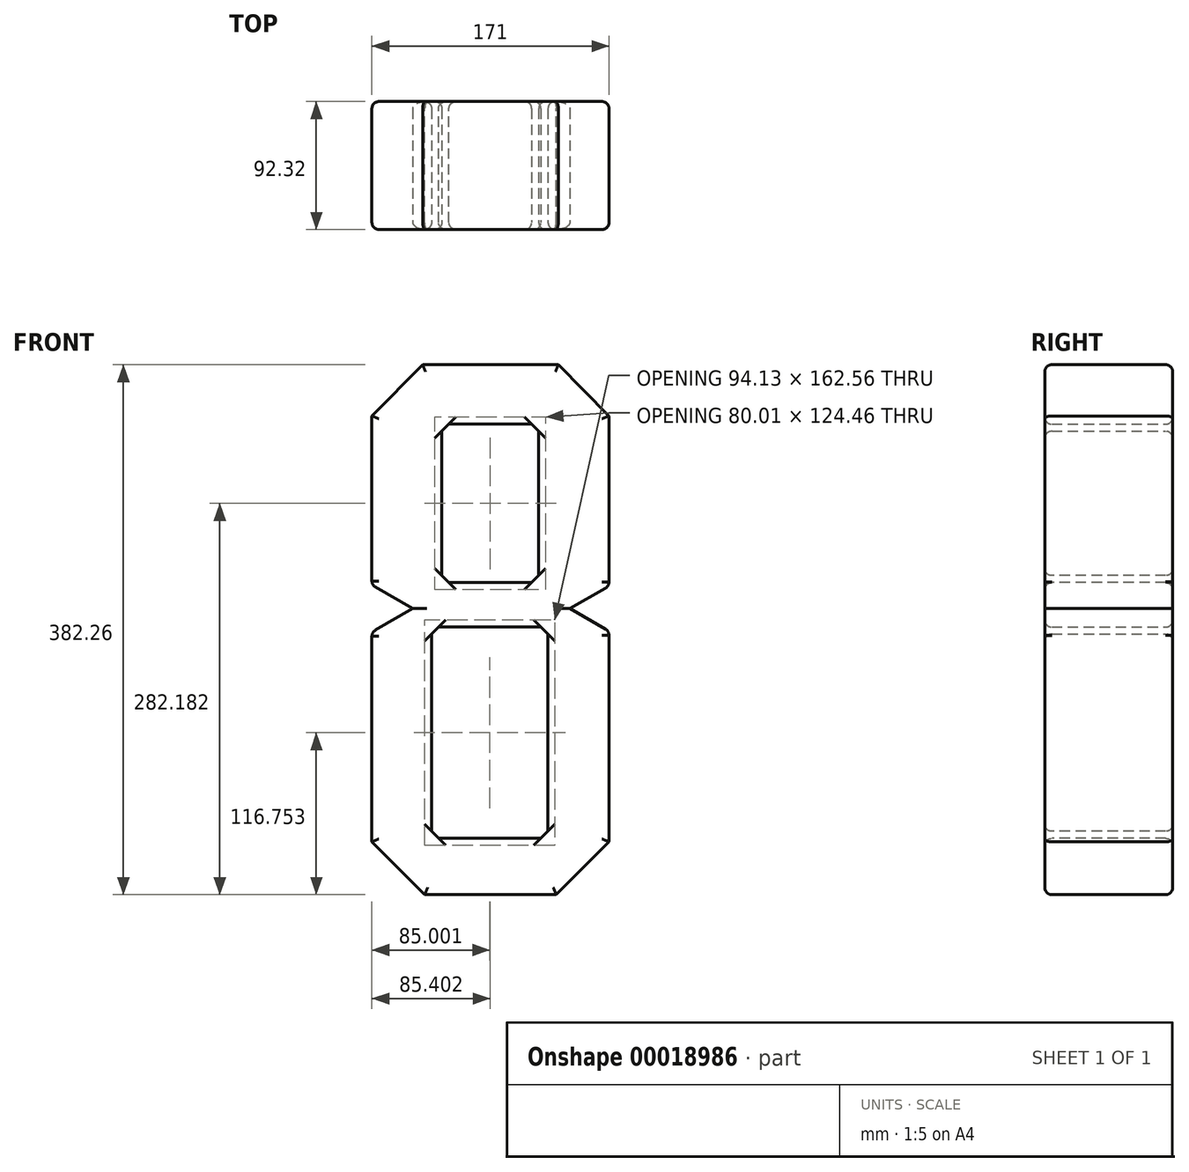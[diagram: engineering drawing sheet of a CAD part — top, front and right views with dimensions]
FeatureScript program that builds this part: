
annotation { "Feature Type Name" : "Feature", "Feature Type Description" : "" }
export const myFeature = defineFeature(function(context is Context, id is Id, definition is map)
    precondition{}
    {
        {
            var Q0;
            Q0=qCreatedBy(makeId("Top.planeOp"),FACE);
            var sketch = newSketch(context, id + "F0", { "sketchPlane" : qUnion([Q0])});
            skLineSegment(sketch, "E0.bottom", {"start": v(-73.79, 22.76) * mm, "end": v(97.2, 22.76) * mm});
            skLineSegment(sketch, "E0.top", {"start": v(-73.79, -22.31) * mm, "end": v(97.2, -22.31) * mm});
            skLineSegment(sketch, "E0.left", {"start": v(-73.79, 22.76) * mm, "end": v(-73.79, -22.31) * mm});
            skLineSegment(sketch, "E0.right", {"start": v(97.2, 22.76) * mm, "end": v(97.2, -22.31) * mm});
            skSolve(sketch);
        }
        {
            var Q0;
            Q0 = qSketchRegion(id + "F0", true);
            extrude(context, id + "F1", {"entities" : qUnion([Q0]), "depth" : 382.26 * mm});
        }
        {
            var Q0;
            Q0=makeQuery(id+"F1.opExtrude","SWEPT_FACE",FACE,{"disambiguationData":[OSD([sQuery(id+"F0.wireOp",EDGE,"E0.bottom")])]});
            var sketch = newSketch(context, id + "F2", { "sketchPlane" : qUnion([Q0])});
            skLineSegment(sketch, "E1.bottom", {"start": v(-46.54, 339.33) * mm, "end": v(23.31, 339.33) * mm});
            skLineSegment(sketch, "E1.top", {"start": v(-46.54, 225.03) * mm, "end": v(23.31, 225.03) * mm});
            skLineSegment(sketch, "E1.left", {"start": v(-46.54, 339.33) * mm, "end": v(-46.54, 225.03) * mm});
            skLineSegment(sketch, "E1.right", {"start": v(23.31, 339.33) * mm, "end": v(23.31, 225.03) * mm});
            skLineSegment(sketch, "E2.bottom", {"start": v(-53.2, 192.95) * mm, "end": v(30.77, 192.95) * mm});
            skLineSegment(sketch, "E2.top", {"start": v(-53.2, 40.55) * mm, "end": v(30.77, 40.55) * mm});
            skLineSegment(sketch, "E2.left", {"start": v(-53.2, 192.95) * mm, "end": v(-53.2, 40.55) * mm});
            skLineSegment(sketch, "E2.right", {"start": v(30.77, 192.95) * mm, "end": v(30.77, 40.55) * mm});
            skSolve(sketch);
        }
        {
            var Q0;
            Q0 = qSketchRegion(id + "F2", true);
            extrude(context, id + "F3", {"entities" : qUnion([Q0]), "operationType" : NewBodyOperationType.REMOVE, "endBound" : BoundingType.THROUGH_ALL, "oppositeDirection" : true, "depth" : 25.4 * mm});
        }
        {
            var Q0;
            Q0=makeQuery(id+"F1.opExtrude","SWEPT_FACE",FACE,{"disambiguationData":[OSD([sQuery(id+"F0.wireOp",EDGE,"E0.bottom")])]});
            var sketch = newSketch(context, id + "F4", { "sketchPlane" : qUnion([Q0])});
            skLineSegment(sketch, "E3", {"start": v(-97.2, 345.3) * mm, "end": v(-97.2, 400.52) * mm});
            skLineSegment(sketch, "E4", {"start": v(-97.2, 400.52) * mm, "end": v(-42.6, 400.52) * mm});
            skLineSegment(sketch, "E5", {"start": v(-42.6, 400.52) * mm, "end": v(-97.2, 345.3) * mm});
            skLineSegment(sketch, "E6", {"start": v(73.79, 345.3) * mm, "end": v(73.79, 400.52) * mm});
            skLineSegment(sketch, "E7", {"start": v(73.79, 400.52) * mm, "end": v(19.18, 400.52) * mm});
            skLineSegment(sketch, "E8", {"start": v(19.18, 400.52) * mm, "end": v(73.79, 345.3) * mm});
            skSolve(sketch);
        }
        {
            var Q0;
            Q0 = qSketchRegion(id + "F4", true);
            extrude(context, id + "F5", {"entities" : qUnion([Q0]), "operationType" : NewBodyOperationType.REMOVE, "endBound" : BoundingType.THROUGH_ALL, "oppositeDirection" : true, "depth" : 25.4 * mm});
        }
        {
            var Q0;
            Q0=makeQuery(id+"F1.opExtrude","SWEPT_FACE",FACE,{"disambiguationData":[OSD([sQuery(id+"F0.wireOp",EDGE,"E0.bottom")])]});
            var sketch = newSketch(context, id + "F6", { "sketchPlane" : qUnion([Q0])});
            skLineSegment(sketch, "E9", {"start": v(-97.2, 38.1) * mm, "end": v(-97.2, 0) * mm});
            skLineSegment(sketch, "E10", {"start": v(-97.2, 0) * mm, "end": v(-59.1, 0) * mm});
            skLineSegment(sketch, "E11", {"start": v(-59.1, 0) * mm, "end": v(-97.2, 38.1) * mm});
            skLineSegment(sketch, "E12", {"start": v(73.79, 38.1) * mm, "end": v(73.79, 0) * mm});
            skLineSegment(sketch, "E13", {"start": v(73.79, 0) * mm, "end": v(35.69, 0) * mm});
            skLineSegment(sketch, "E14", {"start": v(35.69, 0) * mm, "end": v(73.79, 38.1) * mm});
            skSolve(sketch);
        }
        {
            var Q0;
            Q0 = qSketchRegion(id + "F6", true);
            extrude(context, id + "F7", {"entities" : qUnion([Q0]), "operationType" : NewBodyOperationType.REMOVE, "endBound" : BoundingType.THROUGH_ALL, "oppositeDirection" : true, "depth" : 25.4 * mm});
        }
        {
            var Q0;
            Q0=makeQuery(id+"F1.opExtrude","SWEPT_FACE",FACE,{"disambiguationData":[OSD([sQuery(id+"F0.wireOp",EDGE,"E0.bottom")])]});
            extrude(context, id + "F8", {"entities" : qUnion([Q0]), "operationType" : NewBodyOperationType.ADD, "depth" : 47.26 * mm});
        }
        {
            var Q0;
            {var subQ0=sQuery(id+"F2.wireOp",EDGE,"E1.bottom");var subQ1=sQuery(id+"F2.wireOp",EDGE,"E1.right");Q0=makeQuery(id+"F8.boolean.opBoolean","MERGE",EDGE,{"derivedFrom":[makeQuery(id+"F3.boolean.opBoolean","COPY",EDGE,{"derivedFrom":makeQuery(id+"F3.opExtrude","SWEPT_EDGE",EDGE,{"disambiguationData":[OSD([subQ0,subQ1])]})}),makeQuery(id+"F8.opExtrude","SWEPT_EDGE",EDGE,{"disambiguationData":[OSD([subQ0,subQ1])]})]});}
            var Q1;
            {var subQ0=sQuery(id+"F2.wireOp",EDGE,"E1.bottom");var subQ1=sQuery(id+"F2.wireOp",EDGE,"E1.left");Q1=makeQuery(id+"F8.boolean.opBoolean","MERGE",EDGE,{"derivedFrom":[makeQuery(id+"F3.boolean.opBoolean","COPY",EDGE,{"derivedFrom":makeQuery(id+"F3.opExtrude","SWEPT_EDGE",EDGE,{"disambiguationData":[OSD([subQ0,subQ1])]})}),makeQuery(id+"F8.opExtrude","SWEPT_EDGE",EDGE,{"disambiguationData":[OSD([subQ0,subQ1])]})]});}
            var Q2;
            {var subQ0=sQuery(id+"F2.wireOp",EDGE,"E1.top");var subQ1=sQuery(id+"F2.wireOp",EDGE,"E1.right");Q2=makeQuery(id+"F8.boolean.opBoolean","MERGE",EDGE,{"derivedFrom":[makeQuery(id+"F3.boolean.opBoolean","COPY",EDGE,{"derivedFrom":makeQuery(id+"F3.opExtrude","SWEPT_EDGE",EDGE,{"disambiguationData":[OSD([subQ0,subQ1])]})}),makeQuery(id+"F8.opExtrude","SWEPT_EDGE",EDGE,{"disambiguationData":[OSD([subQ0,subQ1])]})]});}
            var Q3;
            {var subQ0=sQuery(id+"F2.wireOp",EDGE,"E1.top");var subQ1=sQuery(id+"F2.wireOp",EDGE,"E1.left");Q3=makeQuery(id+"F8.boolean.opBoolean","MERGE",EDGE,{"derivedFrom":[makeQuery(id+"F3.boolean.opBoolean","COPY",EDGE,{"derivedFrom":makeQuery(id+"F3.opExtrude","SWEPT_EDGE",EDGE,{"disambiguationData":[OSD([subQ0,subQ1])]})}),makeQuery(id+"F8.opExtrude","SWEPT_EDGE",EDGE,{"disambiguationData":[OSD([subQ0,subQ1])]})]});}
            var Q4;
            {var subQ0=sQuery(id+"F2.wireOp",EDGE,"E2.top");var subQ1=sQuery(id+"F2.wireOp",EDGE,"E2.left");Q4=makeQuery(id+"F8.boolean.opBoolean","MERGE",EDGE,{"derivedFrom":[makeQuery(id+"F3.boolean.opBoolean","COPY",EDGE,{"derivedFrom":makeQuery(id+"F3.opExtrude","SWEPT_EDGE",EDGE,{"disambiguationData":[OSD([subQ0,subQ1])]})}),makeQuery(id+"F8.opExtrude","SWEPT_EDGE",EDGE,{"disambiguationData":[OSD([subQ0,subQ1])]})]});}
            var Q5;
            {var subQ0=sQuery(id+"F2.wireOp",EDGE,"E2.bottom");var subQ1=sQuery(id+"F2.wireOp",EDGE,"E2.right");Q5=makeQuery(id+"F8.boolean.opBoolean","MERGE",EDGE,{"derivedFrom":[makeQuery(id+"F3.boolean.opBoolean","COPY",EDGE,{"derivedFrom":makeQuery(id+"F3.opExtrude","SWEPT_EDGE",EDGE,{"disambiguationData":[OSD([subQ0,subQ1])]})}),makeQuery(id+"F8.opExtrude","SWEPT_EDGE",EDGE,{"disambiguationData":[OSD([subQ0,subQ1])]})]});}
            var Q6;
            {var subQ0=sQuery(id+"F2.wireOp",EDGE,"E2.bottom");var subQ1=sQuery(id+"F2.wireOp",EDGE,"E2.left");Q6=makeQuery(id+"F8.boolean.opBoolean","MERGE",EDGE,{"derivedFrom":[makeQuery(id+"F3.boolean.opBoolean","COPY",EDGE,{"derivedFrom":makeQuery(id+"F3.opExtrude","SWEPT_EDGE",EDGE,{"disambiguationData":[OSD([subQ0,subQ1])]})}),makeQuery(id+"F8.opExtrude","SWEPT_EDGE",EDGE,{"disambiguationData":[OSD([subQ0,subQ1])]})]});}
            var Q7;
            {var subQ0=sQuery(id+"F2.wireOp",EDGE,"E2.top");var subQ1=sQuery(id+"F2.wireOp",EDGE,"E2.right");Q7=makeQuery(id+"F8.boolean.opBoolean","MERGE",EDGE,{"derivedFrom":[makeQuery(id+"F3.boolean.opBoolean","COPY",EDGE,{"derivedFrom":makeQuery(id+"F3.opExtrude","SWEPT_EDGE",EDGE,{"disambiguationData":[OSD([subQ0,subQ1])]})}),makeQuery(id+"F8.opExtrude","SWEPT_EDGE",EDGE,{"disambiguationData":[OSD([subQ0,subQ1])]})]});}
            chamfer(context, id + "F9", {"entities" : qUnion([Q0, Q1, Q2, Q3, Q4, Q5, Q6, Q7]), "width" : 5.08 * mm, "tangentPropagation" : true});
        }
        {
            var Q0;
            Q0=makeQuery(id+"F1.opExtrude","SWEPT_EDGE",EDGE,{"disambiguationData":[OSD([sQuery(id+"F0.wireOp",EDGE,"E0.top"),sQuery(id+"F0.wireOp",EDGE,"E0.right")])]});
            var Q1;
            Q1=makeQuery(id+"F1.opExtrude","SWEPT_EDGE",EDGE,{"disambiguationData":[OSD([sQuery(id+"F0.wireOp",EDGE,"E0.top"),sQuery(id+"F0.wireOp",EDGE,"E0.left")])]});
            var Q2;
            Q2=makeQuery(id+"F7.boolean.opBoolean","INTERSECT",EDGE,{"derivedFrom":[makeQuery(id+"F1.opExtrude","SWEPT_FACE",FACE,{"disambiguationData":[OSD([sQuery(id+"F0.wireOp",EDGE,"E0.top")])]}),makeQuery(id+"F7.opExtrude","SWEPT_FACE",FACE,{"disambiguationData":[OSD([sQuery(id+"F6.wireOp",EDGE,"E14")])]})]});
            var Q3;
            Q3=makeQuery(id+"F1.opExtrude","CAP_EDGE",EDGE,{"disambiguationData":[OSD([sQuery(id+"F0.wireOp",EDGE,"E0.top")])],"isStart":true});
            var Q4;
            Q4=makeQuery(id+"F7.boolean.opBoolean","INTERSECT",EDGE,{"derivedFrom":[makeQuery(id+"F1.opExtrude","SWEPT_FACE",FACE,{"disambiguationData":[OSD([sQuery(id+"F0.wireOp",EDGE,"E0.top")])]}),makeQuery(id+"F7.opExtrude","SWEPT_FACE",FACE,{"disambiguationData":[OSD([sQuery(id+"F6.wireOp",EDGE,"E11")])]})]});
            var Q5;
            Q5=makeQuery(id+"F1.opExtrude","CAP_EDGE",EDGE,{"disambiguationData":[OSD([sQuery(id+"F0.wireOp",EDGE,"E0.top")])],"isStart":false});
            var Q6;
            Q6=makeQuery(id+"F5.boolean.opBoolean","INTERSECT",EDGE,{"derivedFrom":[makeQuery(id+"F1.opExtrude","SWEPT_FACE",FACE,{"disambiguationData":[OSD([sQuery(id+"F0.wireOp",EDGE,"E0.top")])]}),makeQuery(id+"F5.opExtrude","SWEPT_FACE",FACE,{"disambiguationData":[OSD([sQuery(id+"F4.wireOp",EDGE,"E5")])]})]});
            var Q7;
            Q7=makeQuery(id+"F5.boolean.opBoolean","INTERSECT",EDGE,{"derivedFrom":[makeQuery(id+"F1.opExtrude","SWEPT_FACE",FACE,{"disambiguationData":[OSD([sQuery(id+"F0.wireOp",EDGE,"E0.top")])]}),makeQuery(id+"F5.opExtrude","SWEPT_FACE",FACE,{"disambiguationData":[OSD([sQuery(id+"F4.wireOp",EDGE,"E8")])]})]});
            var Q8;
            {var subQ0=sQuery(id+"F0.wireOp",EDGE,"E0.bottom");Q8=makeQuery(id+"F8.opExtrude","CAP_EDGE",EDGE,{"disambiguationData":[OSD([subQ0]),TDD([makeQuery(id+"F1.opExtrude","CAP_EDGE",EDGE,{"disambiguationData":[OSD([subQ0])],"isStart":false})])],"isStart":false});}
            var Q9;
            Q9=makeQuery(id+"F8.opExtrude","CAP_EDGE",EDGE,{"disambiguationData":[OSD([sQuery(id+"F4.wireOp",EDGE,"E5")])],"isStart":false});
            var Q10;
            Q10=makeQuery(id+"F8.opExtrude","CAP_EDGE",EDGE,{"disambiguationData":[OSD([sQuery(id+"F4.wireOp",EDGE,"E8")])],"isStart":false});
            var Q11;
            Q11=makeQuery(id+"F8.opExtrude","CAP_EDGE",EDGE,{"disambiguationData":[OSD([sQuery(id+"F0.wireOp",EDGE,"E0.bottom"),sQuery(id+"F0.wireOp",EDGE,"E0.left")])],"isStart":false});
            var Q12;
            Q12=makeQuery(id+"F8.opExtrude","CAP_EDGE",EDGE,{"disambiguationData":[OSD([sQuery(id+"F6.wireOp",EDGE,"E14")])],"isStart":false});
            var Q13;
            {var subQ0=sQuery(id+"F0.wireOp",EDGE,"E0.bottom");Q13=makeQuery(id+"F8.opExtrude","CAP_EDGE",EDGE,{"disambiguationData":[OSD([subQ0]),TDD([makeQuery(id+"F1.opExtrude","CAP_EDGE",EDGE,{"disambiguationData":[OSD([subQ0])],"isStart":true})])],"isStart":false});}
            var Q14;
            Q14=makeQuery(id+"F8.opExtrude","CAP_EDGE",EDGE,{"disambiguationData":[OSD([sQuery(id+"F6.wireOp",EDGE,"E11")])],"isStart":false});
            var Q15;
            Q15=makeQuery(id+"F8.opExtrude","CAP_EDGE",EDGE,{"disambiguationData":[OSD([sQuery(id+"F0.wireOp",EDGE,"E0.bottom"),sQuery(id+"F0.wireOp",EDGE,"E0.right")])],"isStart":false});
            fillet(context, id + "F10", {"entities" : qUnion([Q0, Q1, Q2, Q3, Q4, Q5, Q6, Q7, Q8, Q9, Q10, Q11, Q12, Q13, Q14, Q15]), "radius" : 5.08 * mm, "tangentPropagation" : true, "allowEdgeOverflow" : false});
        }
        {
            var Q0;
            Q0=makeQuery(id+"F8.opExtrude","CAP_EDGE",EDGE,{"disambiguationData":[OSD([sQuery(id+"F2.wireOp",EDGE,"E1.left")])],"isStart":false});
            var Q1;
            Q1=makeQuery(id+"F3.boolean.opBoolean","INTERSECT",EDGE,{"derivedFrom":[makeQuery(id+"F1.opExtrude","SWEPT_FACE",FACE,{"disambiguationData":[OSD([sQuery(id+"F0.wireOp",EDGE,"E0.top")])]}),makeQuery(id+"F3.opExtrude","SWEPT_FACE",FACE,{"disambiguationData":[OSD([sQuery(id+"F2.wireOp",EDGE,"E1.bottom")])]})]});
            var Q2;
            Q2=makeQuery(id+"F8.opExtrude","CAP_EDGE",EDGE,{"disambiguationData":[OSD([sQuery(id+"F2.wireOp",EDGE,"E1.right")])],"isStart":false});
            var Q3;
            Q3=makeQuery(id+"F8.opExtrude","CAP_EDGE",EDGE,{"disambiguationData":[OSD([sQuery(id+"F2.wireOp",EDGE,"E1.top")])],"isStart":false});
            var Q4;
            Q4=makeQuery(id+"F8.opExtrude","CAP_EDGE",EDGE,{"disambiguationData":[OSD([sQuery(id+"F2.wireOp",EDGE,"E2.left")])],"isStart":false});
            var Q5;
            Q5=makeQuery(id+"F3.boolean.opBoolean","INTERSECT",EDGE,{"derivedFrom":[makeQuery(id+"F1.opExtrude","SWEPT_FACE",FACE,{"disambiguationData":[OSD([sQuery(id+"F0.wireOp",EDGE,"E0.top")])]}),makeQuery(id+"F3.opExtrude","SWEPT_FACE",FACE,{"disambiguationData":[OSD([sQuery(id+"F2.wireOp",EDGE,"E2.bottom")])]})]});
            var Q6;
            Q6=makeQuery(id+"F8.opExtrude","CAP_EDGE",EDGE,{"disambiguationData":[OSD([sQuery(id+"F2.wireOp",EDGE,"E2.right")])],"isStart":false});
            var Q7;
            Q7=makeQuery(id+"F8.opExtrude","CAP_EDGE",EDGE,{"disambiguationData":[OSD([sQuery(id+"F2.wireOp",EDGE,"E2.top")])],"isStart":false});
            var Q8;
            Q8=makeQuery(id+"F3.boolean.opBoolean","INTERSECT",EDGE,{"derivedFrom":[makeQuery(id+"F1.opExtrude","SWEPT_FACE",FACE,{"disambiguationData":[OSD([sQuery(id+"F0.wireOp",EDGE,"E0.top")])]}),makeQuery(id+"F3.opExtrude","SWEPT_FACE",FACE,{"disambiguationData":[OSD([sQuery(id+"F2.wireOp",EDGE,"E2.left")])]})]});
            var Q9;
            Q9=makeQuery(id+"F3.boolean.opBoolean","INTERSECT",EDGE,{"derivedFrom":[makeQuery(id+"F1.opExtrude","SWEPT_FACE",FACE,{"disambiguationData":[OSD([sQuery(id+"F0.wireOp",EDGE,"E0.top")])]}),makeQuery(id+"F3.opExtrude","SWEPT_FACE",FACE,{"disambiguationData":[OSD([sQuery(id+"F2.wireOp",EDGE,"E2.top")])]})]});
            var Q10;
            Q10=makeQuery(id+"F3.boolean.opBoolean","INTERSECT",EDGE,{"derivedFrom":[makeQuery(id+"F1.opExtrude","SWEPT_FACE",FACE,{"disambiguationData":[OSD([sQuery(id+"F0.wireOp",EDGE,"E0.top")])]}),makeQuery(id+"F3.opExtrude","SWEPT_FACE",FACE,{"disambiguationData":[OSD([sQuery(id+"F2.wireOp",EDGE,"E2.right")])]})]});
            var Q11;
            Q11=makeQuery(id+"F3.boolean.opBoolean","INTERSECT",EDGE,{"derivedFrom":[makeQuery(id+"F1.opExtrude","SWEPT_FACE",FACE,{"disambiguationData":[OSD([sQuery(id+"F0.wireOp",EDGE,"E0.top")])]}),makeQuery(id+"F3.opExtrude","SWEPT_FACE",FACE,{"disambiguationData":[OSD([sQuery(id+"F2.wireOp",EDGE,"E1.right")])]})]});
            var Q12;
            Q12=makeQuery(id+"F3.boolean.opBoolean","INTERSECT",EDGE,{"derivedFrom":[makeQuery(id+"F1.opExtrude","SWEPT_FACE",FACE,{"disambiguationData":[OSD([sQuery(id+"F0.wireOp",EDGE,"E0.top")])]}),makeQuery(id+"F3.opExtrude","SWEPT_FACE",FACE,{"disambiguationData":[OSD([sQuery(id+"F2.wireOp",EDGE,"E1.left")])]})]});
            var Q13;
            Q13=makeQuery(id+"F3.boolean.opBoolean","INTERSECT",EDGE,{"derivedFrom":[makeQuery(id+"F1.opExtrude","SWEPT_FACE",FACE,{"disambiguationData":[OSD([sQuery(id+"F0.wireOp",EDGE,"E0.top")])]}),makeQuery(id+"F3.opExtrude","SWEPT_FACE",FACE,{"disambiguationData":[OSD([sQuery(id+"F2.wireOp",EDGE,"E1.top")])]})]});
            var Q14;
            Q14=makeQuery(id+"F8.opExtrude","CAP_EDGE",EDGE,{"disambiguationData":[OSD([sQuery(id+"F2.wireOp",EDGE,"E1.bottom")])],"isStart":false});
            var Q15;
            Q15=makeQuery(id+"F8.opExtrude","CAP_EDGE",EDGE,{"disambiguationData":[OSD([sQuery(id+"F2.wireOp",EDGE,"E2.bottom")])],"isStart":false});
            fillet(context, id + "F11", {"entities" : qUnion([Q0, Q1, Q2, Q3, Q4, Q5, Q6, Q7, Q8, Q9, Q10, Q11, Q12, Q13, Q14, Q15]), "radius" : 5.08 * mm, "tangentPropagation" : true, "allowEdgeOverflow" : false});
        }
        {
            var Q0;
            Q0=makeQuery(id+"F1.opExtrude","SWEPT_FACE",FACE,{"disambiguationData":[OSD([sQuery(id+"F0.wireOp",EDGE,"E0.top")])]});
            var sketch = newSketch(context, id + "F12", { "sketchPlane" : qUnion([Q0])});
            skLineSegment(sketch, "E15", {"start": v(-44.32, 206.29) * mm, "end": v(-85.02, 229.78) * mm});
            skLineSegment(sketch, "E16", {"start": v(-85.02, 229.78) * mm, "end": v(-85.02, 182.8) * mm});
            skLineSegment(sketch, "E17", {"start": v(-85.02, 182.8) * mm, "end": v(-44.32, 206.29) * mm});
            skLineSegment(sketch, "E18", {"start": v(69, 206.29) * mm, "end": v(109.69, 182.8) * mm});
            skLineSegment(sketch, "E19", {"start": v(109.69, 182.8) * mm, "end": v(109.69, 229.78) * mm});
            skLineSegment(sketch, "E20", {"start": v(109.69, 229.78) * mm, "end": v(69, 206.29) * mm});
            skSolve(sketch);
        }
        {
            var Q0;
            Q0 = qSketchRegion(id + "F12", true);
            extrude(context, id + "F13", {"entities" : qUnion([Q0]), "operationType" : NewBodyOperationType.REMOVE, "endBound" : BoundingType.THROUGH_ALL, "oppositeDirection" : true, "depth" : 25.4 * mm});
        }
        {
            var Q0;
            {var subQ0=sQuery(id+"F0.wireOp",EDGE,"E0.right");Q0=makeQuery(id+"F13.boolean.opBoolean","INTERSECT",EDGE,{"derivedFrom":[makeQuery(id+"F8.boolean.opBoolean","MERGE",FACE,{"derivedFrom":[makeQuery(id+"F1.opExtrude","SWEPT_FACE",FACE,{"disambiguationData":[OSD([subQ0])]}),makeQuery(id+"F8.opExtrude","SWEPT_FACE",FACE,{"disambiguationData":[OSD([sQuery(id+"F0.wireOp",EDGE,"E0.bottom"),subQ0])]})]}),makeQuery(id+"F13.opExtrude","SWEPT_FACE",FACE,{"disambiguationData":[OSD([sQuery(id+"F12.wireOp",EDGE,"E20")])]})]});}
            var Q1;
            {var subQ0=sQuery(id+"F0.wireOp",EDGE,"E0.right");Q1=makeQuery(id+"F13.boolean.opBoolean","INTERSECT",EDGE,{"derivedFrom":[makeQuery(id+"F8.boolean.opBoolean","MERGE",FACE,{"derivedFrom":[makeQuery(id+"F1.opExtrude","SWEPT_FACE",FACE,{"disambiguationData":[OSD([subQ0])]}),makeQuery(id+"F8.opExtrude","SWEPT_FACE",FACE,{"disambiguationData":[OSD([sQuery(id+"F0.wireOp",EDGE,"E0.bottom"),subQ0])]})]}),makeQuery(id+"F13.opExtrude","SWEPT_FACE",FACE,{"disambiguationData":[OSD([sQuery(id+"F12.wireOp",EDGE,"E18")])]})]});}
            var Q2;
            {var subQ0=sQuery(id+"F0.wireOp",EDGE,"E0.left");Q2=makeQuery(id+"F13.boolean.opBoolean","INTERSECT",EDGE,{"derivedFrom":[makeQuery(id+"F8.boolean.opBoolean","MERGE",FACE,{"derivedFrom":[makeQuery(id+"F1.opExtrude","SWEPT_FACE",FACE,{"disambiguationData":[OSD([subQ0])]}),makeQuery(id+"F8.opExtrude","SWEPT_FACE",FACE,{"disambiguationData":[OSD([sQuery(id+"F0.wireOp",EDGE,"E0.bottom"),subQ0])]})]}),makeQuery(id+"F13.opExtrude","SWEPT_FACE",FACE,{"disambiguationData":[OSD([sQuery(id+"F12.wireOp",EDGE,"E15")])]})]});}
            var Q3;
            {var subQ0=sQuery(id+"F0.wireOp",EDGE,"E0.left");Q3=makeQuery(id+"F13.boolean.opBoolean","INTERSECT",EDGE,{"derivedFrom":[makeQuery(id+"F8.boolean.opBoolean","MERGE",FACE,{"derivedFrom":[makeQuery(id+"F1.opExtrude","SWEPT_FACE",FACE,{"disambiguationData":[OSD([subQ0])]}),makeQuery(id+"F8.opExtrude","SWEPT_FACE",FACE,{"disambiguationData":[OSD([sQuery(id+"F0.wireOp",EDGE,"E0.bottom"),subQ0])]})]}),makeQuery(id+"F13.opExtrude","SWEPT_FACE",FACE,{"disambiguationData":[OSD([sQuery(id+"F12.wireOp",EDGE,"E17")])]})]});}
            fillet(context, id + "F14", {"entities" : qUnion([Q0, Q1, Q2, Q3]), "radius" : 5.08 * mm, "tangentPropagation" : true, "allowEdgeOverflow" : false});
        }
    });
